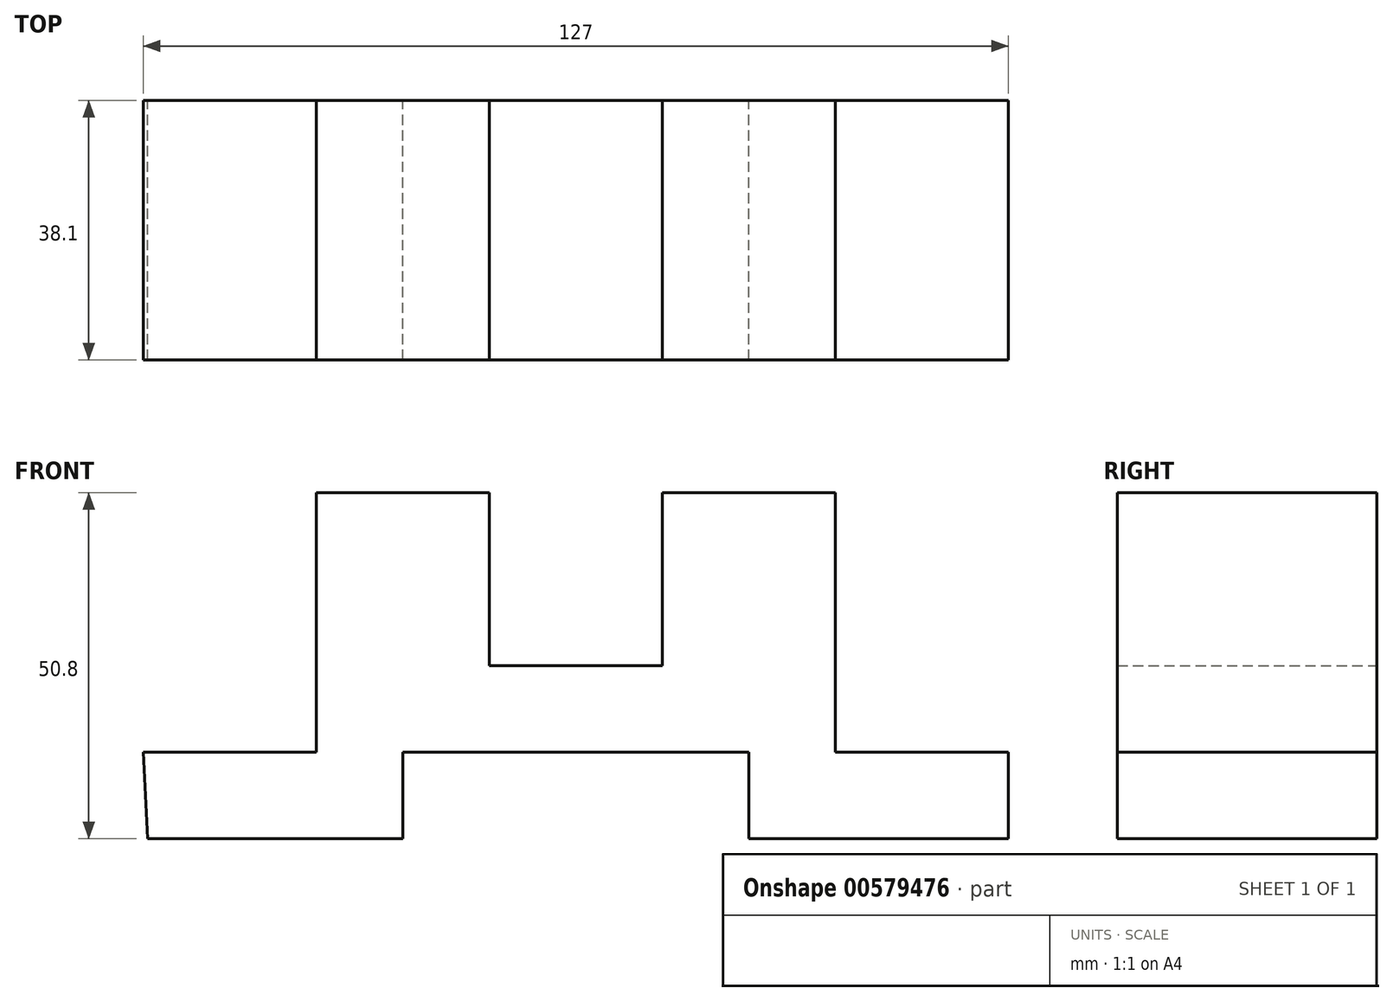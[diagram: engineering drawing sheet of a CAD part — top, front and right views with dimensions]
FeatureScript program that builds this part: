
annotation { "Feature Type Name" : "Feature", "Feature Type Description" : "" }
export const myFeature = defineFeature(function(context is Context, id is Id, definition is map)
    precondition{}
    {
        {
            var Q0;
            Q0=qCreatedBy(makeId("Front.planeOp"),FACE);
            var sketch = newSketch(context, id + "F0", { "sketchPlane" : qUnion([Q0])});
            skLineSegment(sketch, "E0", {"start": v(-63.82, -32.73) * mm, "end": v(-26.33, -32.73) * mm});
            skLineSegment(sketch, "E1", {"start": v(-26.33, -32.73) * mm, "end": v(-26.33, -20.03) * mm});
            skLineSegment(sketch, "E2", {"start": v(-26.33, -20.03) * mm, "end": v(24.47, -20.03) * mm});
            skLineSegment(sketch, "E3", {"start": v(24.47, -20.03) * mm, "end": v(24.47, -32.73) * mm});
            skLineSegment(sketch, "E4", {"start": v(24.47, -32.73) * mm, "end": v(62.57, -32.73) * mm});
            skLineSegment(sketch, "E5", {"start": v(62.57, -32.73) * mm, "end": v(62.57, -20.03) * mm});
            skLineSegment(sketch, "E6", {"start": v(62.57, -20.03) * mm, "end": v(37.17, -20.03) * mm});
            skLineSegment(sketch, "E7", {"start": v(37.17, -20.03) * mm, "end": v(37.17, 18.07) * mm});
            skLineSegment(sketch, "E8", {"start": v(37.17, 18.07) * mm, "end": v(11.77, 18.07) * mm});
            skLineSegment(sketch, "E9", {"start": v(11.77, 18.07) * mm, "end": v(11.77, -7.33) * mm});
            skLineSegment(sketch, "E10", {"start": v(11.77, -7.33) * mm, "end": v(-13.63, -7.33) * mm});
            skLineSegment(sketch, "E11", {"start": v(-13.63, -7.33) * mm, "end": v(-13.63, 18.07) * mm});
            skLineSegment(sketch, "E12", {"start": v(-13.63, 18.07) * mm, "end": v(-39.03, 18.07) * mm});
            skLineSegment(sketch, "E13", {"start": v(-39.03, 18.07) * mm, "end": v(-39.03, -20.03) * mm});
            skLineSegment(sketch, "E14", {"start": v(-39.03, -20.03) * mm, "end": v(-64.43, -20.03) * mm});
            skLineSegment(sketch, "E15", {"start": v(-64.43, -20.03) * mm, "end": v(-63.82, -32.73) * mm});
            skSolve(sketch);
        }
        {
            var Q0;
            Q0=makeQuery(id+"F0.imprint","IMPRINT",FACE,{"disambiguationData":[TD([[makeQuery(id+"F0.imprint","IMPRINT",EDGE,{"derivedFrom":sQuery(id+"F0.wireOp",EDGE,"E0")}),1.0]])]});
            extrude(context, id + "F1", {"entities" : qUnion([Q0]), "depth" : 38.1 * mm, "offsetDistance" : 25.4 * mm});
        }
    });
